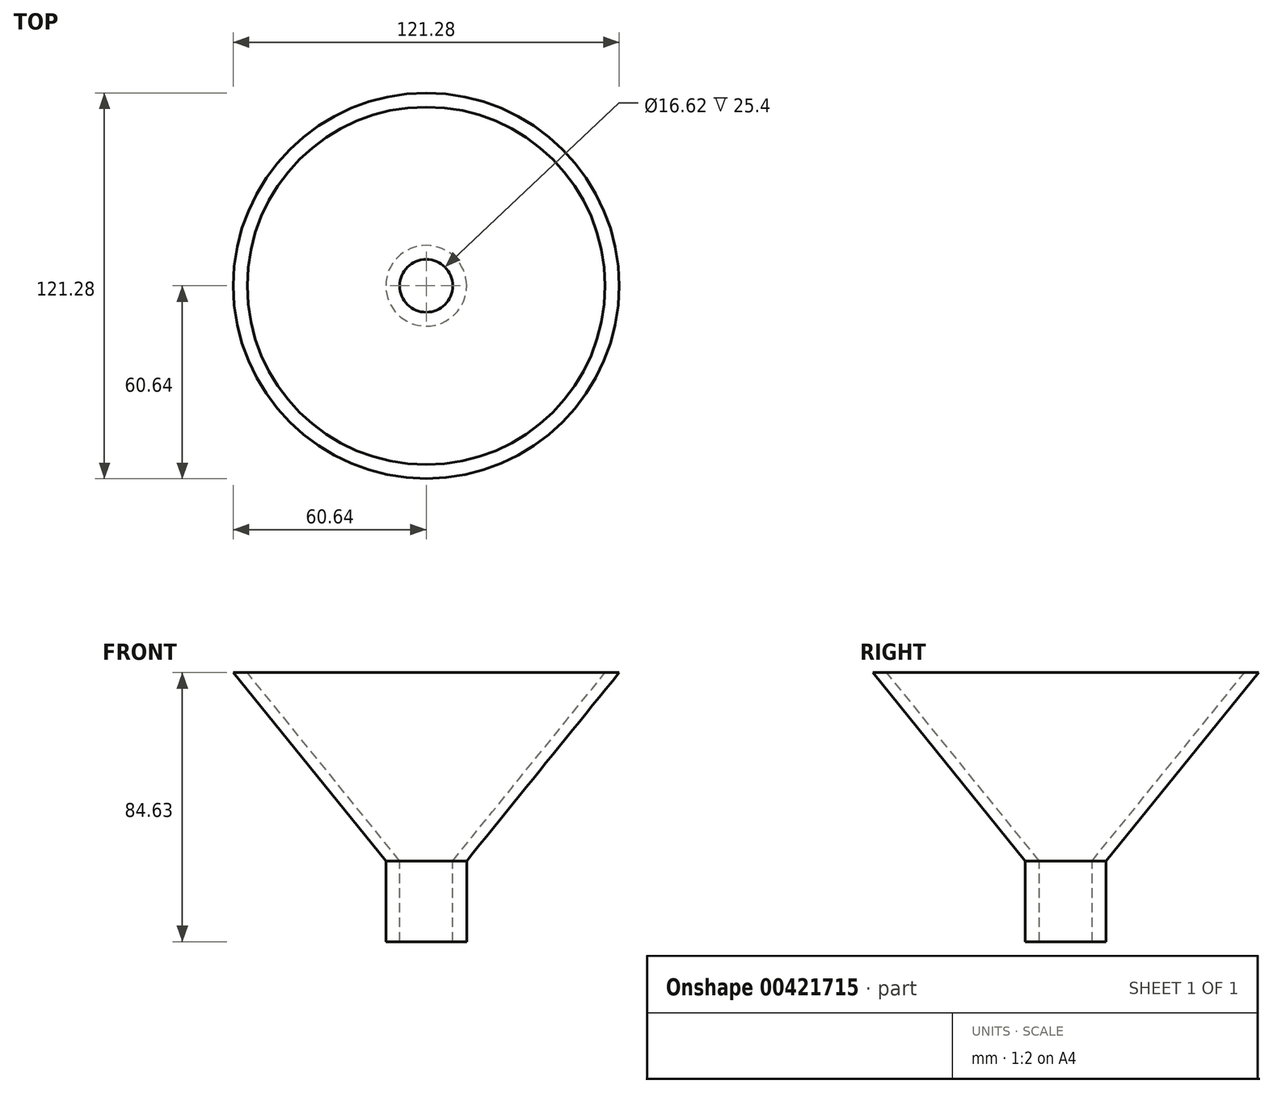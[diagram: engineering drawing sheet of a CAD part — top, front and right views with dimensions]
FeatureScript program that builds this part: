
annotation { "Feature Type Name" : "Feature", "Feature Type Description" : "" }
export const myFeature = defineFeature(function(context is Context, id is Id, definition is map)
    precondition{}
    {
        {
            var Q0;
            Q0=qCreatedBy(makeId("Front.planeOp"),FACE);
            var sketch = newSketch(context, id + "F0", { "sketchPlane" : qUnion([Q0])});
            skLineSegment(sketch, "E0", {"start": v(0, 0) * mm, "end": v(0, -25.4) * mm});
            skLineSegment(sketch, "E1", {"start": v(0, -25.4) * mm, "end": v(12.7, -25.4) * mm});
            skLineSegment(sketch, "E2", {"start": v(12.7, -25.4) * mm, "end": v(12.7, 0) * mm});
            skLineSegment(sketch, "E3", {"start": v(12.7, 0) * mm, "end": v(60.64, 59.23) * mm});
            skLineSegment(sketch, "E4", {"start": v(60.64, 59.23) * mm, "end": v(56.25, 59.23) * mm});
            skLineSegment(sketch, "E5", {"start": v(56.25, 59.23) * mm, "end": v(8.3, 0) * mm});
            skLineSegment(sketch, "E6", {"start": v(8.3, 0) * mm, "end": v(0, 0) * mm});
            skSolve(sketch);
        }
        {
            var Q0;
            Q0=makeQuery(id+"F0.imprint","IMPRINT",FACE,{"disambiguationData":[TD([[makeQuery(id+"F0.imprint","IMPRINT",EDGE,{"derivedFrom":sQuery(id+"F0.wireOp",EDGE,"E0")}),1.0]])]});
            var Q1;
            Q1=sQuery(id+"F0.wireOp",EDGE,"E0");
            revolve(context, id + "F1", {"entities" : qUnion([Q0]), "axis" : qUnion([Q1]), "revolveType" : RevolveType.FULL});
        }
        {
            var Q0;
            Q0=makeQuery(id+"F1.opRevolve","SWEPT_FACE",FACE,{"disambiguationData":[OSD([sQuery(id+"F0.wireOp",EDGE,"E6")])]});
            extrude(context, id + "F2", {"entities" : qUnion([Q0]), "operationType" : NewBodyOperationType.REMOVE, "oppositeDirection" : true, "depth" : 50.8 * mm});
        }
    });
